annotation { "Feature Type Name" : "Feature", "Feature Type Description" : "" }
export const myFeature = defineFeature(function(context is Context, id is Id, definition is map)
    precondition{}
    {
        {
            assignVariable(context, id + "F0", {"name" : "ESPESOR", "anyValue" : 3});
        }
        {
            var Q0;
            Q0=qCreatedBy(makeId("Top.planeOp"),FACE);
            var sketch = newSketch(context, id + "F1", { "sketchPlane" : qUnion([Q0])});
            skText(sketch, "E0", { "text": "CATERINA", "fontName": "AllertaStencil-Regular.ttf"});
            skText(sketch, "E1", { "text": "MARTIN\n", "fontName": "AllertaStencil-Regular.ttf"});
            skText(sketch, "E2", { "text": "ANA Y ANGEL", "fontName": "AllertaStencil-Regular.ttf"});
            skText(sketch, "E3", { "text": "VICTORIA Y FRANCISCO", "fontName": "AllertaStencil-Regular.ttf"});
            skText(sketch, "E4", { "text": "BEA Y ALBERTO", "fontName": "AllertaStencil-Regular.ttf"});
            skLineSegment(sketch, "E5.bottom", {"start": v(335.53, 465) * mm, "end": v(-20, 465) * mm});
            skLineSegment(sketch, "E5.top", {"start": v(335.53, 380) * mm, "end": v(-20, 380) * mm});
            skLineSegment(sketch, "E5.left", {"start": v(335.53, 465) * mm, "end": v(335.53, 380) * mm});
            skLineSegment(sketch, "E5.right", {"start": v(-20, 465) * mm, "end": v(-20, 380) * mm});
            skPoint(sketch, "E5.middle", {"position": v(157.76, 422.5) * mm});
            skLineSegment(sketch, "E6.bottom", {"start": v(261, 370) * mm, "end": v(-20, 370) * mm});
            skLineSegment(sketch, "E6.top", {"start": v(261, 285) * mm, "end": v(-20, 285) * mm});
            skLineSegment(sketch, "E6.left", {"start": v(261, 370) * mm, "end": v(261, 285) * mm});
            skLineSegment(sketch, "E6.right", {"start": v(-20, 370) * mm, "end": v(-20, 285) * mm});
            skPoint(sketch, "E6.middle", {"position": v(120.5, 327.5) * mm});
            skLineSegment(sketch, "E7.bottom", {"start": v(439.5, 275) * mm, "end": v(-20, 275) * mm});
            skLineSegment(sketch, "E7.top", {"start": v(439.5, 190) * mm, "end": v(-20, 190) * mm});
            skLineSegment(sketch, "E7.left", {"start": v(439.5, 275) * mm, "end": v(439.5, 190) * mm});
            skLineSegment(sketch, "E7.right", {"start": v(-20, 275) * mm, "end": v(-20, 190) * mm});
            skPoint(sketch, "E7.middle", {"position": v(209.75, 232.5) * mm});
            skLineSegment(sketch, "E8.bottom", {"start": v(737.84, 180) * mm, "end": v(-20, 180) * mm});
            skLineSegment(sketch, "E8.top", {"start": v(737.84, 95) * mm, "end": v(-20, 95) * mm});
            skLineSegment(sketch, "E8.left", {"start": v(737.84, 180) * mm, "end": v(737.84, 95) * mm});
            skLineSegment(sketch, "E8.right", {"start": v(-20, 180) * mm, "end": v(-20, 95) * mm});
            skPoint(sketch, "E8.middle", {"position": v(358.92, 137.5) * mm});
            skLineSegment(sketch, "E9.bottom", {"start": v(507.42, 85) * mm, "end": v(-20, 85) * mm});
            skLineSegment(sketch, "E9.top", {"start": v(507.42, 0) * mm, "end": v(-20, 0) * mm});
            skLineSegment(sketch, "E9.left", {"start": v(507.42, 85) * mm, "end": v(507.42, 0) * mm});
            skLineSegment(sketch, "E9.right", {"start": v(-20, 85) * mm, "end": v(-20, 0) * mm});
            skPoint(sketch, "E9.middle", {"position": v(243.71, 42.5) * mm});
            skText(sketch, "E10", { "text": "ZHENIA", "fontName": "AllertaStencil-Regular.ttf"});
            skLineSegment(sketch, "E11.bottom", {"start": v(252.57, 560) * mm, "end": v(-20, 560) * mm});
            skLineSegment(sketch, "E11.top", {"start": v(252.57, 475) * mm, "end": v(-20, 475) * mm});
            skLineSegment(sketch, "E11.left", {"start": v(252.57, 560) * mm, "end": v(252.57, 475) * mm});
            skLineSegment(sketch, "E11.right", {"start": v(-20, 560) * mm, "end": v(-20, 475) * mm});
            skPoint(sketch, "E11.middle", {"position": v(116.28, 517.5) * mm});
            skText(sketch, "E12", { "text": "LUSCAS", "fontName": "AllertaStencil-Regular.ttf"});
            skLineSegment(sketch, "E13.bottom", {"start": v(547.24, 370) * mm, "end": v(271, 370) * mm});
            skLineSegment(sketch, "E13.top", {"start": v(547.24, 285) * mm, "end": v(271, 285) * mm});
            skLineSegment(sketch, "E13.left", {"start": v(547.24, 370) * mm, "end": v(547.24, 285) * mm});
            skLineSegment(sketch, "E13.right", {"start": v(271, 370) * mm, "end": v(271, 285) * mm});
            skPoint(sketch, "E13.middle", {"position": v(409.12, 327.5) * mm});
            skLineSegment(sketch, "E14", {"start": v(270.75, 467.16) * mm, "end": v(358.6, 555) * mm});
            skLineSegment(sketch, "E15", {"start": v(358.6, 555) * mm, "end": v(358.6, 473.16) * mm});
            skLineSegment(sketch, "E16", {"start": v(358.6, 473.16) * mm, "end": v(361.6, 473.16) * mm});
            skLineSegment(sketch, "E17", {"start": v(361.6, 473.16) * mm, "end": v(361.6, 510.4) * mm});
            skLineSegment(sketch, "E18", {"start": v(361.6, 510.4) * mm, "end": v(365.6, 510.4) * mm});
            skLineSegment(sketch, "E19", {"start": v(365.6, 510.4) * mm, "end": v(365.6, 467.16) * mm});
            skLineSegment(sketch, "E20", {"start": v(365.6, 467.16) * mm, "end": v(270.75, 467.16) * mm});
            skLineSegment(sketch, "E21", {"start": v(0, 495) * mm, "end": v(-20, 495) * mm, "construction": true});
            skPoint(sketch, "E22", {"position": v(-10, 495) * mm});
            skLineSegment(sketch, "E23", {"start": v(232.57, 495) * mm, "end": v(252.57, 495) * mm, "construction": true});
            skLineSegment(sketch, "E24", {"start": v(315.53, 400) * mm, "end": v(335.53, 400) * mm, "construction": true});
            skLineSegment(sketch, "E25", {"start": v(0, 305) * mm, "end": v(-20, 305) * mm, "construction": true});
            skPoint(sketch, "E26", {"position": v(-10, 305) * mm});
            skLineSegment(sketch, "E27", {"start": v(241, 305) * mm, "end": v(261, 305) * mm, "construction": true});
            skLineSegment(sketch, "E28", {"start": v(271, 305) * mm, "end": v(291, 305) * mm, "construction": true});
            skLineSegment(sketch, "E29", {"start": v(527.24, 305) * mm, "end": v(547.24, 305) * mm, "construction": true});
            skLineSegment(sketch, "E30", {"start": v(419.5, 210) * mm, "end": v(439.5, 210) * mm, "construction": true});
            skLineSegment(sketch, "E31", {"start": v(717.84, 115) * mm, "end": v(737.84, 115) * mm, "construction": true});
            skLineSegment(sketch, "E32", {"start": v(487.42, 20) * mm, "end": v(507.42, 20) * mm, "construction": true});
            skLineSegment(sketch, "E33", {"start": v(0, 20) * mm, "end": v(-20, 20) * mm, "construction": true});
            skLineSegment(sketch, "E34", {"start": v(0, 210) * mm, "end": v(-20, 210) * mm, "construction": true});
            skLineSegment(sketch, "E35", {"start": v(0, 115) * mm, "end": v(-20, 115) * mm, "construction": true});
            skLineSegment(sketch, "E36", {"start": v(0, 400) * mm, "end": v(-20, 400) * mm, "construction": true});
            skLineSegment(sketch, "E37.bottom", {"start": v(-8.5, 380) * mm, "end": v(-11.5, 380) * mm});
            skLineSegment(sketch, "E37.top", {"start": v(-8.5, 386) * mm, "end": v(-11.5, 386) * mm});
            skLineSegment(sketch, "E37.left", {"start": v(-8.5, 380) * mm, "end": v(-8.5, 386) * mm});
            skLineSegment(sketch, "E37.right", {"start": v(-11.5, 380) * mm, "end": v(-11.5, 386) * mm});
            skPoint(sketch, "E37.middle", {"position": v(-10, 383) * mm});
            skPoint(sketch, "E37.middle.positionSnap0", {"position": v(-10, 400) * mm});
            skPoint(sketch, "E37.centerSnap0", {"position": v(-10, 400) * mm});
            skLineSegment(sketch, "E38.bottom", {"start": v(-8.5, 475) * mm, "end": v(-11.5, 475) * mm});
            skLineSegment(sketch, "E38.top", {"start": v(-8.5, 481) * mm, "end": v(-11.5, 481) * mm});
            skLineSegment(sketch, "E38.left", {"start": v(-8.5, 475) * mm, "end": v(-8.5, 481) * mm});
            skLineSegment(sketch, "E38.right", {"start": v(-11.5, 475) * mm, "end": v(-11.5, 481) * mm});
            skPoint(sketch, "E38.middle", {"position": v(-10, 478) * mm});
            skLineSegment(sketch, "E39.bottom", {"start": v(-11.5, 285) * mm, "end": v(-8.5, 285) * mm});
            skLineSegment(sketch, "E39.top", {"start": v(-11.5, 291) * mm, "end": v(-8.5, 291) * mm});
            skLineSegment(sketch, "E39.left", {"start": v(-11.5, 285) * mm, "end": v(-11.5, 291) * mm});
            skLineSegment(sketch, "E39.right", {"start": v(-8.5, 285) * mm, "end": v(-8.5, 291) * mm});
            skLineSegment(sketch, "E40.bottom", {"start": v(-8.5, 190) * mm, "end": v(-11.5, 190) * mm});
            skLineSegment(sketch, "E40.top", {"start": v(-8.5, 196) * mm, "end": v(-11.5, 196) * mm});
            skLineSegment(sketch, "E40.left", {"start": v(-8.5, 190) * mm, "end": v(-8.5, 196) * mm});
            skLineSegment(sketch, "E40.right", {"start": v(-11.5, 190) * mm, "end": v(-11.5, 196) * mm});
            skLineSegment(sketch, "E41.bottom", {"start": v(-11.5, 95) * mm, "end": v(-8.5, 95) * mm});
            skLineSegment(sketch, "E41.top", {"start": v(-11.5, 101) * mm, "end": v(-8.5, 101) * mm});
            skLineSegment(sketch, "E41.left", {"start": v(-11.5, 95) * mm, "end": v(-11.5, 101) * mm});
            skLineSegment(sketch, "E41.right", {"start": v(-8.5, 95) * mm, "end": v(-8.5, 101) * mm});
            skLineSegment(sketch, "E42.bottom", {"start": v(-11.5, 0) * mm, "end": v(-8.5, 0) * mm});
            skLineSegment(sketch, "E42.top", {"start": v(-11.5, 6) * mm, "end": v(-8.5, 6) * mm});
            skLineSegment(sketch, "E42.left", {"start": v(-11.5, 0) * mm, "end": v(-11.5, 6) * mm});
            skLineSegment(sketch, "E42.right", {"start": v(-8.5, 0) * mm, "end": v(-8.5, 6) * mm});
            skPoint(sketch, "E43", {"position": v(497.42, 20) * mm});
            skPoint(sketch, "E44", {"position": v(727.84, 115) * mm});
            skPoint(sketch, "E45", {"position": v(429.5, 210) * mm});
            skPoint(sketch, "E46", {"position": v(537.24, 305) * mm});
            skPoint(sketch, "E47", {"position": v(325.53, 400) * mm});
            skPoint(sketch, "E48", {"position": v(242.57, 495) * mm});
            skLineSegment(sketch, "E49", {"start": v(265.88, 463.7) * mm, "end": v(263.17, 461) * mm});
            skLineSegment(sketch, "E50.MirrorCS", {"start": v(269.34, 468.57) * mm, "end": v(357.18, 556.41) * mm});
            skLineSegment(sketch, "E51.MirrorCS", {"start": v(269.34, 563.41) * mm, "end": v(269.34, 468.57) * mm});
            skLineSegment(sketch, "E52.MirrorCS", {"start": v(312.58, 563.41) * mm, "end": v(269.34, 563.41) * mm});
            skLineSegment(sketch, "E53.MirrorCS", {"start": v(275.34, 559.41) * mm, "end": v(312.58, 559.41) * mm});
            skLineSegment(sketch, "E54.MirrorCS", {"start": v(275.34, 556.41) * mm, "end": v(275.34, 559.41) * mm});
            skLineSegment(sketch, "E55.MirrorCS", {"start": v(357.18, 556.41) * mm, "end": v(275.34, 556.41) * mm});
            skLineSegment(sketch, "E56.MirrorCS", {"start": v(312.58, 559.41) * mm, "end": v(312.58, 563.41) * mm});
            skLineSegment(sketch, "E57", {"start": v(556.24, 188) * mm, "end": v(644.08, 275.84) * mm});
            skLineSegment(sketch, "E58", {"start": v(644.08, 275.84) * mm, "end": v(644.08, 194) * mm});
            skLineSegment(sketch, "E59", {"start": v(644.08, 194) * mm, "end": v(647.08, 194) * mm});
            skLineSegment(sketch, "E60", {"start": v(647.08, 194) * mm, "end": v(647.08, 231.25) * mm});
            skLineSegment(sketch, "E61", {"start": v(647.08, 231.25) * mm, "end": v(651.08, 231.25) * mm});
            skLineSegment(sketch, "E62", {"start": v(651.08, 231.25) * mm, "end": v(651.08, 188) * mm});
            skLineSegment(sketch, "E63", {"start": v(651.08, 188) * mm, "end": v(556.24, 188) * mm});
            skLineSegment(sketch, "E64.MirrorCS", {"start": v(554.82, 189.41) * mm, "end": v(642.66, 277.26) * mm});
            skLineSegment(sketch, "E65.MirrorCS", {"start": v(554.82, 284.26) * mm, "end": v(554.82, 189.41) * mm});
            skLineSegment(sketch, "E66.MirrorCS", {"start": v(598.07, 284.26) * mm, "end": v(554.82, 284.26) * mm});
            skLineSegment(sketch, "E67.MirrorCS", {"start": v(560.82, 280.26) * mm, "end": v(598.07, 280.26) * mm});
            skLineSegment(sketch, "E68.MirrorCS", {"start": v(560.82, 277.26) * mm, "end": v(560.82, 280.26) * mm});
            skLineSegment(sketch, "E69.MirrorCS", {"start": v(642.66, 277.26) * mm, "end": v(560.82, 277.26) * mm});
            skLineSegment(sketch, "E70.MirrorCS", {"start": v(598.07, 280.26) * mm, "end": v(598.07, 284.26) * mm});
            skLineSegment(sketch, "E71", {"start": v(391.68, 381) * mm, "end": v(479.52, 468.84) * mm});
            skLineSegment(sketch, "E72", {"start": v(479.52, 468.84) * mm, "end": v(479.52, 387) * mm});
            skLineSegment(sketch, "E73", {"start": v(479.52, 387) * mm, "end": v(482.52, 387) * mm});
            skLineSegment(sketch, "E74", {"start": v(482.52, 387) * mm, "end": v(482.52, 424.25) * mm});
            skLineSegment(sketch, "E75", {"start": v(482.52, 424.25) * mm, "end": v(486.52, 424.25) * mm});
            skLineSegment(sketch, "E76", {"start": v(486.52, 424.25) * mm, "end": v(486.52, 381) * mm});
            skLineSegment(sketch, "E77", {"start": v(486.52, 381) * mm, "end": v(391.68, 381) * mm});
            skLineSegment(sketch, "E78.MirrorCS", {"start": v(390.27, 382.41) * mm, "end": v(478.1, 470.26) * mm});
            skLineSegment(sketch, "E79.MirrorCS", {"start": v(390.27, 477.26) * mm, "end": v(390.27, 382.41) * mm});
            skLineSegment(sketch, "E80.MirrorCS", {"start": v(433.51, 477.26) * mm, "end": v(390.27, 477.26) * mm});
            skLineSegment(sketch, "E81.MirrorCS", {"start": v(396.27, 473.26) * mm, "end": v(433.51, 473.26) * mm});
            skLineSegment(sketch, "E82.MirrorCS", {"start": v(396.27, 470.26) * mm, "end": v(396.27, 473.26) * mm});
            skLineSegment(sketch, "E83.MirrorCS", {"start": v(478.1, 470.26) * mm, "end": v(396.27, 470.26) * mm});
            skLineSegment(sketch, "E84.MirrorCS", {"start": v(433.51, 473.26) * mm, "end": v(433.51, 477.26) * mm});
            skLineSegment(sketch, "E85", {"start": v(497.52, 381) * mm, "end": v(585.36, 468.84) * mm});
            skLineSegment(sketch, "E86", {"start": v(585.36, 468.84) * mm, "end": v(585.36, 387) * mm});
            skLineSegment(sketch, "E87", {"start": v(585.36, 387) * mm, "end": v(588.36, 387) * mm});
            skLineSegment(sketch, "E88", {"start": v(588.36, 387) * mm, "end": v(588.36, 424.25) * mm});
            skLineSegment(sketch, "E89", {"start": v(588.36, 424.25) * mm, "end": v(592.36, 424.25) * mm});
            skLineSegment(sketch, "E90", {"start": v(592.36, 424.25) * mm, "end": v(592.36, 381) * mm});
            skLineSegment(sketch, "E91", {"start": v(592.36, 381) * mm, "end": v(497.52, 381) * mm});
            skLineSegment(sketch, "E92.MirrorCS", {"start": v(496.1, 382.41) * mm, "end": v(583.95, 470.26) * mm});
            skLineSegment(sketch, "E93.MirrorCS", {"start": v(496.1, 477.26) * mm, "end": v(496.1, 382.41) * mm});
            skLineSegment(sketch, "E94.MirrorCS", {"start": v(539.35, 477.26) * mm, "end": v(496.1, 477.26) * mm});
            skLineSegment(sketch, "E95.MirrorCS", {"start": v(502.1, 473.26) * mm, "end": v(539.35, 473.26) * mm});
            skLineSegment(sketch, "E96.MirrorCS", {"start": v(502.1, 470.26) * mm, "end": v(502.1, 473.26) * mm});
            skLineSegment(sketch, "E97.MirrorCS", {"start": v(583.95, 470.26) * mm, "end": v(502.1, 470.26) * mm});
            skLineSegment(sketch, "E98.MirrorCS", {"start": v(539.35, 473.26) * mm, "end": v(539.35, 477.26) * mm});
            skLineSegment(sketch, "E99", {"start": v(598.7, 381) * mm, "end": v(686.54, 468.84) * mm});
            skLineSegment(sketch, "E100", {"start": v(686.54, 468.84) * mm, "end": v(686.54, 387) * mm});
            skLineSegment(sketch, "E101", {"start": v(686.54, 387) * mm, "end": v(689.54, 387) * mm});
            skLineSegment(sketch, "E102", {"start": v(689.54, 387) * mm, "end": v(689.54, 424.25) * mm});
            skLineSegment(sketch, "E103", {"start": v(689.54, 424.25) * mm, "end": v(693.54, 424.25) * mm});
            skLineSegment(sketch, "E104", {"start": v(693.54, 424.25) * mm, "end": v(693.54, 381) * mm});
            skLineSegment(sketch, "E105", {"start": v(693.54, 381) * mm, "end": v(598.7, 381) * mm});
            skLineSegment(sketch, "E106.MirrorCS", {"start": v(597.29, 382.41) * mm, "end": v(685.13, 470.26) * mm});
            skLineSegment(sketch, "E107.MirrorCS", {"start": v(597.29, 477.26) * mm, "end": v(597.29, 382.41) * mm});
            skLineSegment(sketch, "E108.MirrorCS", {"start": v(640.53, 477.26) * mm, "end": v(597.29, 477.26) * mm});
            skLineSegment(sketch, "E109.MirrorCS", {"start": v(603.29, 473.26) * mm, "end": v(640.53, 473.26) * mm});
            skLineSegment(sketch, "E110.MirrorCS", {"start": v(603.29, 470.26) * mm, "end": v(603.29, 473.26) * mm});
            skLineSegment(sketch, "E111.MirrorCS", {"start": v(685.13, 470.26) * mm, "end": v(603.29, 470.26) * mm});
            skLineSegment(sketch, "E112.MirrorCS", {"start": v(640.53, 473.26) * mm, "end": v(640.53, 477.26) * mm});
            const initialGuessF1  = {"E0": [0, 0.4, 1, 0, 0.045], "E1": [0, 0.305, 1, 0, 0.045], "E2": [0, 0.21, 1, 0, 0.045], "E3": [0, 0.115, 1, 0, 0.045], "E4": [0, 0.02, 1, 0, 0.045], "E10": [0, 0.495, 1, 0, 0.045], "E12": [0.291, 0.305, 1, 0, 0.045]};
            skSetInitialGuess(sketch, initialGuessF1);
            skSolve(sketch);
        }
        {
            var Q0;
            Q0=makeQuery(id+"F1.imprint","IMPRINT",FACE,{"disambiguationData":[TD([[makeQuery(id+"F1.imprint","IMPRINT",EDGE,{"derivedFrom":sQuery(id+"F1.wireOp",EDGE,"E0.sketch_text.stroke-0")}),1.0]])]});
            var Q1;
            Q1=makeQuery(id+"F1.imprint","IMPRINT",FACE,{"disambiguationData":[TD([[makeQuery(id+"F1.imprint","IMPRINT",EDGE,{"derivedFrom":sQuery(id+"F1.wireOp",EDGE,"E1.sketch_text.stroke-0")}),1.0]])]});
            var Q2;
            Q2=makeQuery(id+"F1.imprint","IMPRINT",FACE,{"disambiguationData":[TD([[makeQuery(id+"F1.imprint","IMPRINT",EDGE,{"derivedFrom":sQuery(id+"F1.wireOp",EDGE,"E2.sketch_text.stroke-0")}),1.0]])]});
            var Q3;
            Q3=makeQuery(id+"F1.imprint","IMPRINT",FACE,{"disambiguationData":[TD([[makeQuery(id+"F1.imprint","IMPRINT",EDGE,{"derivedFrom":sQuery(id+"F1.wireOp",EDGE,"E3.sketch_text.stroke-0")}),1.0]])]});
            var Q4;
            Q4=makeQuery(id+"F1.imprint","IMPRINT",FACE,{"disambiguationData":[TD([[makeQuery(id+"F1.imprint","IMPRINT",EDGE,{"derivedFrom":sQuery(id+"F1.wireOp",EDGE,"E4.sketch_text.stroke-0")}),1.0]])]});
            var Q5;
            Q5=makeQuery(id+"F1.imprint","IMPRINT",FACE,{"disambiguationData":[TD([[makeQuery(id+"F1.imprint","IMPRINT",EDGE,{"derivedFrom":sQuery(id+"F1.wireOp",EDGE,"E10.sketch_text.stroke-0")}),1.0]])]});
            var Q6;
            Q6=makeQuery(id+"F1.imprint","IMPRINT",FACE,{"disambiguationData":[TD([[makeQuery(id+"F1.imprint","IMPRINT",EDGE,{"derivedFrom":sQuery(id+"F1.wireOp",EDGE,"E12.sketch_text.stroke-0")}),1.0]])]});
            var Q7;
            Q7=makeQuery(id+"F1.imprint","IMPRINT",FACE,{"disambiguationData":[TD([[makeQuery(id+"F1.imprint","IMPRINT",EDGE,{"derivedFrom":sQuery(id+"F1.wireOp",EDGE,"E14")}),-1.0]])]});
            var Q8;
            Q8=makeQuery(id+"F1.imprint","IMPRINT",FACE,{"disambiguationData":[TD([[makeQuery(id+"F1.imprint","IMPRINT",EDGE,{"derivedFrom":sQuery(id+"F1.wireOp",EDGE,"E78.MirrorCS")}),1.0]])]});
            var Q9;
            Q9=makeQuery(id+"F1.imprint","IMPRINT",FACE,{"disambiguationData":[TD([[makeQuery(id+"F1.imprint","IMPRINT",EDGE,{"derivedFrom":sQuery(id+"F1.wireOp",EDGE,"E71")}),-1.0]])]});
            var Q10;
            Q10=makeQuery(id+"F1.imprint","IMPRINT",FACE,{"disambiguationData":[TD([[makeQuery(id+"F1.imprint","IMPRINT",EDGE,{"derivedFrom":sQuery(id+"F1.wireOp",EDGE,"E92.MirrorCS")}),1.0]])]});
            var Q11;
            Q11=makeQuery(id+"F1.imprint","IMPRINT",FACE,{"disambiguationData":[TD([[makeQuery(id+"F1.imprint","IMPRINT",EDGE,{"derivedFrom":sQuery(id+"F1.wireOp",EDGE,"E85")}),-1.0]])]});
            var Q12;
            Q12=makeQuery(id+"F1.imprint","IMPRINT",FACE,{"disambiguationData":[TD([[makeQuery(id+"F1.imprint","IMPRINT",EDGE,{"derivedFrom":sQuery(id+"F1.wireOp",EDGE,"E106.MirrorCS")}),1.0]])]});
            var Q13;
            Q13=makeQuery(id+"F1.imprint","IMPRINT",FACE,{"disambiguationData":[TD([[makeQuery(id+"F1.imprint","IMPRINT",EDGE,{"derivedFrom":sQuery(id+"F1.wireOp",EDGE,"E99")}),-1.0]])]});
            var Q14;
            Q14=makeQuery(id+"F1.imprint","IMPRINT",FACE,{"disambiguationData":[TD([[makeQuery(id+"F1.imprint","IMPRINT",EDGE,{"derivedFrom":sQuery(id+"F1.wireOp",EDGE,"E50.MirrorCS")}),1.0]])]});
            var Q15;
            Q15=makeQuery(id+"F1.imprint","IMPRINT",FACE,{"disambiguationData":[TD([[makeQuery(id+"F1.imprint","IMPRINT",EDGE,{"derivedFrom":sQuery(id+"F1.wireOp",EDGE,"E64.MirrorCS")}),1.0]])]});
            var Q16;
            Q16=makeQuery(id+"F1.imprint","IMPRINT",FACE,{"disambiguationData":[TD([[makeQuery(id+"F1.imprint","IMPRINT",EDGE,{"derivedFrom":sQuery(id+"F1.wireOp",EDGE,"E57")}),-1.0]])]});
            extrude(context, id + "F2", {"entities" : qUnion([Q0, Q1, Q2, Q3, Q4, Q5, Q6, Q7, Q8, Q9, Q10, Q11, Q12, Q13, Q14, Q15, Q16]), "depth" : (getVariable(context, 'ESPESOR')) * mm, "offsetDistance" : 25 * mm});
        }
        {
            var Q0;
            Q0=makeQuery(id+"F2.opExtrude","SWEPT_EDGE",EDGE,{"disambiguationData":[OSD([sQuery(id+"F1.wireOp",EDGE,"E5.bottom"),sQuery(id+"F1.wireOp",EDGE,"E5.right")])]});
            var Q1;
            Q1=makeQuery(id+"F2.opExtrude","SWEPT_EDGE",EDGE,{"disambiguationData":[OSD([sQuery(id+"F1.wireOp",EDGE,"E6.bottom"),sQuery(id+"F1.wireOp",EDGE,"E6.right")])]});
            var Q2;
            Q2=makeQuery(id+"F2.opExtrude","SWEPT_EDGE",EDGE,{"disambiguationData":[OSD([sQuery(id+"F1.wireOp",EDGE,"E7.bottom"),sQuery(id+"F1.wireOp",EDGE,"E7.right")])]});
            var Q3;
            Q3=makeQuery(id+"F2.opExtrude","SWEPT_EDGE",EDGE,{"disambiguationData":[OSD([sQuery(id+"F1.wireOp",EDGE,"E8.bottom"),sQuery(id+"F1.wireOp",EDGE,"E8.right")])]});
            var Q4;
            Q4=makeQuery(id+"F2.opExtrude","SWEPT_EDGE",EDGE,{"disambiguationData":[OSD([sQuery(id+"F1.wireOp",EDGE,"E9.bottom"),sQuery(id+"F1.wireOp",EDGE,"E9.right")])]});
            var Q5;
            Q5=makeQuery(id+"F2.opExtrude","SWEPT_EDGE",EDGE,{"disambiguationData":[OSD([sQuery(id+"F1.wireOp",EDGE,"E9.bottom"),sQuery(id+"F1.wireOp",EDGE,"E9.left")])]});
            var Q6;
            Q6=makeQuery(id+"F2.opExtrude","SWEPT_EDGE",EDGE,{"disambiguationData":[OSD([sQuery(id+"F1.wireOp",EDGE,"E9.top"),sQuery(id+"F1.wireOp",EDGE,"E9.left")])]});
            var Q7;
            Q7=makeQuery(id+"F2.opExtrude","SWEPT_EDGE",EDGE,{"disambiguationData":[OSD([sQuery(id+"F1.wireOp",EDGE,"E9.top"),sQuery(id+"F1.wireOp",EDGE,"E9.right")])]});
            var Q8;
            Q8=makeQuery(id+"F2.opExtrude","SWEPT_EDGE",EDGE,{"disambiguationData":[OSD([sQuery(id+"F1.wireOp",EDGE,"E8.top"),sQuery(id+"F1.wireOp",EDGE,"E8.right")])]});
            var Q9;
            Q9=makeQuery(id+"F2.opExtrude","SWEPT_EDGE",EDGE,{"disambiguationData":[OSD([sQuery(id+"F1.wireOp",EDGE,"E8.top"),sQuery(id+"F1.wireOp",EDGE,"E8.left")])]});
            var Q10;
            Q10=makeQuery(id+"F2.opExtrude","SWEPT_EDGE",EDGE,{"disambiguationData":[OSD([sQuery(id+"F1.wireOp",EDGE,"E8.bottom"),sQuery(id+"F1.wireOp",EDGE,"E8.left")])]});
            var Q11;
            Q11=makeQuery(id+"F2.opExtrude","SWEPT_EDGE",EDGE,{"disambiguationData":[OSD([sQuery(id+"F1.wireOp",EDGE,"E7.top"),sQuery(id+"F1.wireOp",EDGE,"E7.right")])]});
            var Q12;
            Q12=makeQuery(id+"F2.opExtrude","SWEPT_EDGE",EDGE,{"disambiguationData":[OSD([sQuery(id+"F1.wireOp",EDGE,"E7.top"),sQuery(id+"F1.wireOp",EDGE,"E7.left")])]});
            var Q13;
            Q13=makeQuery(id+"F2.opExtrude","SWEPT_EDGE",EDGE,{"disambiguationData":[OSD([sQuery(id+"F1.wireOp",EDGE,"E7.bottom"),sQuery(id+"F1.wireOp",EDGE,"E7.left")])]});
            var Q14;
            Q14=makeQuery(id+"F2.opExtrude","SWEPT_EDGE",EDGE,{"disambiguationData":[OSD([sQuery(id+"F1.wireOp",EDGE,"E6.top"),sQuery(id+"F1.wireOp",EDGE,"E6.left")])]});
            var Q15;
            Q15=makeQuery(id+"F2.opExtrude","SWEPT_EDGE",EDGE,{"disambiguationData":[OSD([sQuery(id+"F1.wireOp",EDGE,"E6.bottom"),sQuery(id+"F1.wireOp",EDGE,"E6.left")])]});
            var Q16;
            Q16=makeQuery(id+"F2.opExtrude","SWEPT_EDGE",EDGE,{"disambiguationData":[OSD([sQuery(id+"F1.wireOp",EDGE,"E5.top"),sQuery(id+"F1.wireOp",EDGE,"E5.left")])]});
            var Q17;
            Q17=makeQuery(id+"F2.opExtrude","SWEPT_EDGE",EDGE,{"disambiguationData":[OSD([sQuery(id+"F1.wireOp",EDGE,"E5.bottom"),sQuery(id+"F1.wireOp",EDGE,"E5.left")])]});
            var Q18;
            Q18=makeQuery(id+"F2.opExtrude","SWEPT_EDGE",EDGE,{"disambiguationData":[OSD([sQuery(id+"F1.wireOp",EDGE,"E5.top"),sQuery(id+"F1.wireOp",EDGE,"E5.right")])]});
            var Q19;
            Q19=makeQuery(id+"F2.opExtrude","SWEPT_EDGE",EDGE,{"disambiguationData":[OSD([sQuery(id+"F1.wireOp",EDGE,"E6.top"),sQuery(id+"F1.wireOp",EDGE,"E6.right")])]});
            var Q20;
            Q20=makeQuery(id+"F2.opExtrude","SWEPT_EDGE",EDGE,{"disambiguationData":[OSD([sQuery(id+"F1.wireOp",EDGE,"E11.top"),sQuery(id+"F1.wireOp",EDGE,"E11.right")])]});
            var Q21;
            Q21=makeQuery(id+"F2.opExtrude","SWEPT_EDGE",EDGE,{"disambiguationData":[OSD([sQuery(id+"F1.wireOp",EDGE,"E11.top"),sQuery(id+"F1.wireOp",EDGE,"E11.left")])]});
            var Q22;
            Q22=makeQuery(id+"F2.opExtrude","SWEPT_EDGE",EDGE,{"disambiguationData":[OSD([sQuery(id+"F1.wireOp",EDGE,"E11.bottom"),sQuery(id+"F1.wireOp",EDGE,"E11.left")])]});
            var Q23;
            Q23=makeQuery(id+"F2.opExtrude","SWEPT_EDGE",EDGE,{"disambiguationData":[OSD([sQuery(id+"F1.wireOp",EDGE,"E11.bottom"),sQuery(id+"F1.wireOp",EDGE,"E11.right")])]});
            var Q24;
            Q24=makeQuery(id+"F2.opExtrude","SWEPT_EDGE",EDGE,{"disambiguationData":[OSD([sQuery(id+"F1.wireOp",EDGE,"E13.top"),sQuery(id+"F1.wireOp",EDGE,"E13.left")])]});
            var Q25;
            Q25=makeQuery(id+"F2.opExtrude","SWEPT_EDGE",EDGE,{"disambiguationData":[OSD([sQuery(id+"F1.wireOp",EDGE,"E13.bottom"),sQuery(id+"F1.wireOp",EDGE,"E13.left")])]});
            var Q26;
            Q26=makeQuery(id+"F2.opExtrude","SWEPT_EDGE",EDGE,{"disambiguationData":[OSD([sQuery(id+"F1.wireOp",EDGE,"E13.bottom"),sQuery(id+"F1.wireOp",EDGE,"E13.right")])]});
            var Q27;
            Q27=makeQuery(id+"F2.opExtrude","SWEPT_EDGE",EDGE,{"disambiguationData":[OSD([sQuery(id+"F1.wireOp",EDGE,"E13.top"),sQuery(id+"F1.wireOp",EDGE,"E13.right")])]});
            fillet(context, id + "F3", {"entities" : qUnion([Q0, Q1, Q2, Q3, Q4, Q5, Q6, Q7, Q8, Q9, Q10, Q11, Q12, Q13, Q14, Q15, Q16, Q17, Q18, Q19, Q20, Q21, Q22, Q23, Q24, Q25, Q26, Q27]), "radius" : 10 * mm, "tangentPropagation" : true, "allowEdgeOverflow" : false});
        }
    });